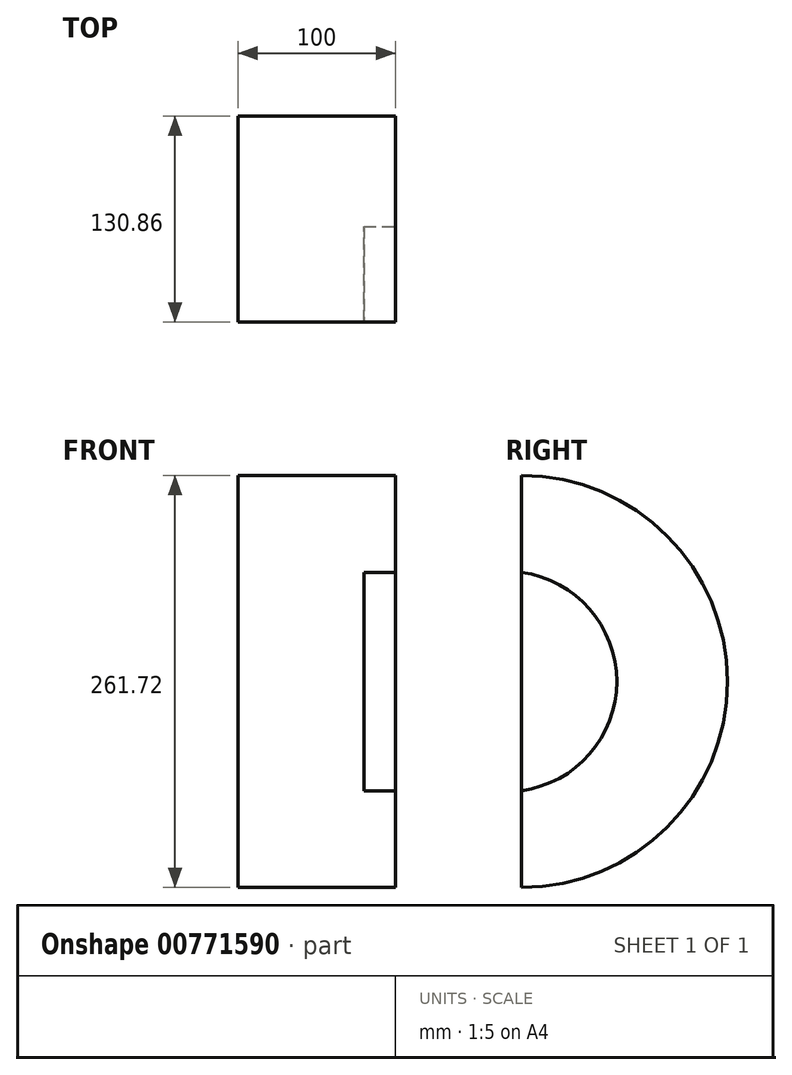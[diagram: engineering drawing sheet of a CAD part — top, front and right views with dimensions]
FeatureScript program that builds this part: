
annotation { "Feature Type Name" : "Feature", "Feature Type Description" : "" }
export const myFeature = defineFeature(function(context is Context, id is Id, definition is map)
    precondition{}
    {
        {
            var Q0;
            Q0=qCreatedBy(makeId("Right.planeOp"),FACE);
            var sketch = newSketch(context, id + "F0", { "sketchPlane" : qUnion([Q0])});
            skCircle(sketch, "E0", {"center": v(0, 0) * mm, "radius": 130.86 * mm});
            skSolve(sketch);
        }
        {
            var Q0;
            Q0 = qSketchRegion(id + "F0", true);
            extrude(context, id + "F1", {"entities" : qUnion([Q0]), "depth" : 100 * mm, "offsetDistance" : 25 * mm});
        }
        {
            var Q0;
            Q0=makeQuery(id+"F1.opExtrude","CAP_FACE",FACE,{"disambiguationData":[OSD([sQuery(id+"F0.wireOp",EDGE,"E0")])],"isStart":false});
            var sketch = newSketch(context, id + "F2", { "sketchPlane" : qUnion([Q0])});
            skCircle(sketch, "E1", {"center": v(-9.42, 0) * mm, "radius": 70 * mm});
            skSolve(sketch);
        }
        {
            var Q0;
            Q0 = qSketchRegion(id + "F2", true);
            extrude(context, id + "F3", {"entities" : qUnion([Q0]), "operationType" : NewBodyOperationType.REMOVE, "oppositeDirection" : true, "depth" : 20 * mm, "offsetDistance" : 25 * mm});
        }
        {
            var Q0;
            Q0=qCreatedBy(makeId("Front.planeOp"),FACE);
            var sketch = newSketch(context, id + "F4", { "sketchPlane" : qUnion([Q0])});
            skLineSegment(sketch, "E2.bottom", {"start": v(-110.04, 170.01) * mm, "end": v(199.95, 170.01) * mm});
            skLineSegment(sketch, "E2.top", {"start": v(-110.04, -164.94) * mm, "end": v(199.95, -164.94) * mm});
            skLineSegment(sketch, "E2.left", {"start": v(-110.04, 170.01) * mm, "end": v(-110.04, -164.94) * mm});
            skLineSegment(sketch, "E2.right", {"start": v(199.95, 170.01) * mm, "end": v(199.95, -164.94) * mm});
            skSolve(sketch);
        }
        {
            var Q0;
            Q0 = qSketchRegion(id + "F4", true);
            extrude(context, id + "F5", {"entities" : qUnion([Q0]), "operationType" : NewBodyOperationType.REMOVE, "depth" : 150 * mm, "offsetDistance" : 25 * mm});
        }
    });
